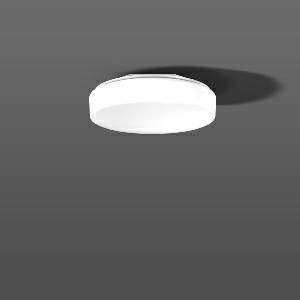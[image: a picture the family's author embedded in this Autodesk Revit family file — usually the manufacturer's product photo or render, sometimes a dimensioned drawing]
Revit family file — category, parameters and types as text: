
# Revit family: flat_polymero_kreis_672092_002_5_1_3bbd
name_source: partatom
category: Lighting Fixtures
units: mm (PartAtom-declared; Revit-internal decimal feet)

## family parameters
Cut with Voids When Loaded = No
Host = Face
Light Source = No
Part Type = Normal
Room Calculation Point = No
Round Connector Dimension = Use Diameter
Shared = No

## types (1)
- FLAT POLYMERO KREIS (1 x LED Modul 840, 1750 lm, 4000)
    Apparent Load = 15 VA
    CIE Flux Codes = 41 71 90 82 100
    Color Rendering = 80
    Color Temperature = 4000
    Default Elevation = 1800 mm
    Description = Series: FLAT POLYMERO KREIS
Decorative round surface-mounted luminaire. For escape route illumination. Base: metal, powder-coated. Diffuser made of non-yellowing plastic (PMMA), opal. Diffuser fastening: patented push system. Suitable for Ceiling mounting, Wall (surface). Electronic ballast included. Self-contained system with automatic self-test. 
Colour: white
Diameter: 360 mm
Height: 109 mm
Weight: 1.88 kg
Operating mode: Combined NL readiness
Duration time: 3 h
Lamp: LED
Socket: without socket
Colour temperature: 4000K
Colour rendering index (CRI): 80
System power: 15 W
Rated luminous flux: 1750 lm
Luminous flux, emergency: 200 lm
System power, emergency: -
Control gear: Regulated power supply
Protection class: I
Type of protection: IP 40
    Height = 109 mm
    Lamp = 1 x LED Modul 840
    Lamp Light Flux = 1750 lm
    Lamp count = 1
    Length = 360 mm
    Lifetime = 50000 h
    Luminous efficacy = 117 lm/W
    Manufacturer = RZB
    ModVariant = No
    Model = 672092.002.5.1
    Mounting Place = Ceiling
    Mounting Type = Surface mounted
    Number of Poles = 1
    OnlyDefault = Yes
    Power Factor = 1
    Product Name = FLAT POLYMERO KREIS
    Product group = Surface mounted ceiling and wall luminaires
    ProductGroupID = 305
    Protection Class = Protection class I
    Protection Degree = Degree of protection
    RLX_Detail_Level = 1
    RLX_Emergency_Light_Flux = 200 lm
    RLX_Emergency_Type = 3
    RLX_Emergency_Type_DB = Yes
    RlxData = <blob elided: 51593 chars, md5=7ce3e00a>
    Socket = socket
    Standby Power = 0 W
    System Light Flux = 1750 lm
    System Power = 15 W
    Type Comments = Product without accessories
    Type Image = 672092.002.1.jpg
    URL = http://relux.com
    VarID = ---
    Voltage = 0 V
    Weight = 0.00 kg
    Width = 0 mm  [stored 0 ft]

note: [stored X ft] marks values corroborated as IEEE doubles in the binary element streams (Revit-internal decimal feet)

## geometry (parser evidence)
native form markers: Blend x4, Sweep x15
no freeform markers — native parametric forms only
